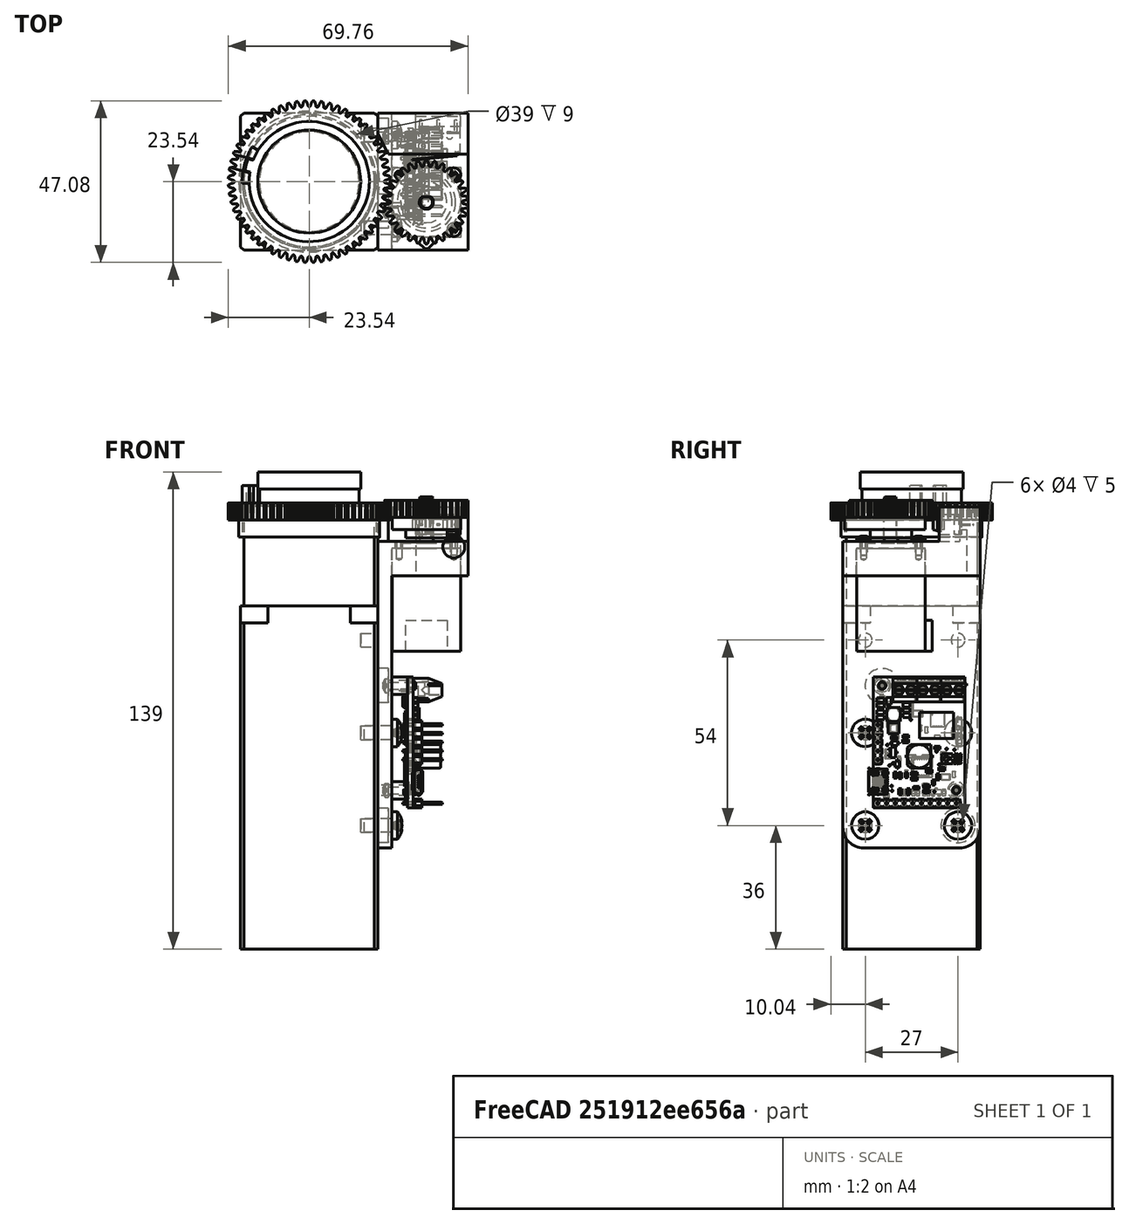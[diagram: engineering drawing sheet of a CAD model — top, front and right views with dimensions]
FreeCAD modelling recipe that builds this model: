
FCSTD DOCUMENT  (FreeCAD 0.19R23578 (Git))
Label: assembly-gear
License: All rights reserved
LicenseURL: http://en.wikipedia.org/wiki/All_rights_reserved
objects: Part::FeaturePython×15, App::FeaturePython×8
note: 15 computed .brp shape members not serialized (recipe doc carries the construction recipe); baked Part::Feature solids carry a one-line shape summary decoded from their .brp

FEATURE [Part::FeaturePython] b_microscope_001_  label="microscope_001"  # a2plus imported part (geometry in sourceFile) (typed FeaturePython)
  Visibility1 = true
  a2p_Version = V0.1
  fixedPosition = true
  objectType = a2pPart
  sourceFile = ./microscope.FCStd
  subassemblyImport = false
  timeLastImport = 1.60829e+09
  updateColors = true
FEATURE [Part::FeaturePython] b_motor_001_  label="motor_001"  # a2plus imported part (geometry in sourceFile) (typed FeaturePython)
  Placement = pos=(34.1,-6,-13.25) rot=(0,0,-1;1.5708rad)
  Visibility1 = true
  a2p_Version = V0.1
  fixedPosition = false
  objectType = a2pPart
  sourceFile = ./motor.FCStd
  subassemblyImport = false
  timeLastImport = 1.60829e+09
  updateColors = true
FEATURE [Part::FeaturePython] b_frame_001_  label="frame_001"  # a2plus imported part (geometry in sourceFile) (typed FeaturePython)
  Placement = pos=(20,-7.61e-14,18.75) rot=(0,0,1;0rad)
  Visibility1 = true
  a2p_Version = V0.1
  fixedPosition = false
  objectType = a2pPart
  sourceFile = ./frame.FCStd
  subassemblyImport = false
  timeLastImport = 1.60978e+09
  updateColors = true
FEATURE [Part::FeaturePython] b_D2FS_FL_N1_001_  label="D2FS_FL_N1_001"  # a2plus imported part (geometry in sourceFile) (typed FeaturePython)
  Placement = pos=(34.35,13,20.75) rot=(0,0,1;3.14159rad)
  Visibility1 = true
  a2p_Version = V0.1
  fixedPosition = false
  objectType = a2pPart
  sourceFile = ./D2FS_FL_N.step
  subassemblyImport = false
  timeLastImport = 1.60829e+09
  updateColors = true
FEATURE [Part::FeaturePython] b_tic834_001_  label="tic834_001"  # a2plus imported part (geometry in sourceFile) (typed FeaturePython)
  Placement = pos=(28.6611,15.54,-58.81) rot=(0.707107,0,0.707107;3.14159rad)
  Visibility1 = true
  a2p_Version = V0.1
  fixedPosition = false
  objectType = a2pPart
  sourceFile = ./tic834.FCStd
  subassemblyImport = false
  timeLastImport = 1.60829e+09
  updateColors = true
FEATURE [Part::FeaturePython] Screw  label="M2x4-Screw"  # Fasteners workbench fastener (typed FeaturePython)
  Placement = pos=(42.1,-14,18.75) rot=(0,0,1;0rad)
  Visibility1 = true
  diameter = 2
  invert = false
  length = 1
  lengthCustom = 4
  matchOuter = false
  offset = 0
  thread = false
  type = 33
FEATURE [Part::FeaturePython] Screw001  label="M2x4-Screw001"  # Fasteners workbench fastener (typed FeaturePython)
  Placement = pos=(42.1,2,18.75) rot=(0,0,1;0rad)
  Visibility1 = true
  diameter = 2
  invert = false
  length = 1
  lengthCustom = 4
  matchOuter = false
  offset = 0
  thread = false
  type = 33
FEATURE [Part::FeaturePython] Screw002  label="M2x8-Screw006"  # Fasteners workbench fastener (typed FeaturePython)
  Placement = pos=(23,-8.59,-23.25) rot=(-0.687002,-0.236764,0.687002;2.67663rad)
  Visibility1 = true
  diameter = 2
  invert = false
  length = 4
  lengthCustom = 8
  matchOuter = false
  offset = 0
  thread = false
  type = 33
FEATURE [Part::FeaturePython] Screw003  label="M4x8-Screw"  # Fasteners workbench fastener (typed FeaturePython)
  Placement = pos=(24,-13.5,-37) rot=(0,1,0;1.5708rad)
  Visibility1 = true
  diameter = 6
  invert = false
  length = 2
  lengthCustom = 8
  matchOuter = false
  offset = 0
  thread = false
  type = 33
FEATURE [Part::FeaturePython] Screw004  label="M4x8-Screw019"  # Fasteners workbench fastener (typed FeaturePython)
  Placement = pos=(24,13.5,-37) rot=(0,1,0;1.5708rad)
  Visibility1 = true
  diameter = 6
  invert = false
  length = 2
  lengthCustom = 8
  matchOuter = false
  offset = 0
  thread = false
  type = 33
FEATURE [Part::FeaturePython] Screw005  label="M4x8-Screw013"  # Fasteners workbench fastener (typed FeaturePython)
  Placement = pos=(24,13.5,-64) rot=(0,1,0;1.5708rad)
  Visibility1 = true
  diameter = 6
  invert = false
  length = 2
  lengthCustom = 8
  matchOuter = false
  offset = 0
  thread = false
  type = 33
FEATURE [Part::FeaturePython] Screw006  label="M4x8-Screw020"  # Fasteners workbench fastener (typed FeaturePython)
  Placement = pos=(24,-13.5,-64) rot=(0,1,0;1.5708rad)
  Visibility1 = true
  diameter = 6
  invert = false
  length = 2
  lengthCustom = 8
  matchOuter = false
  offset = 0
  thread = false
  type = 33
FEATURE [Part::FeaturePython] Screw007  label="M2x8-Screw"  # Fasteners workbench fastener (typed FeaturePython)
  Placement = pos=(23,13,-53.73) rot=(-0.687002,-0.236764,0.687002;2.67663rad)
  Visibility1 = true
  diameter = 2
  invert = false
  length = 4
  lengthCustom = 8
  matchOuter = false
  offset = 0
  thread = false
  type = 33
FEATURE [Part::FeaturePython] b_ring_gear_001_  label="ring-gear_001"  # a2plus imported part (geometry in sourceFile) (typed FeaturePython)
  Placement = pos=(1.33e-13,-2.8158e-12,30) rot=(0,0,1;6.02139rad)
  a2p_Version = V0.1
  fixedPosition = false
  objectType = a2pPart
  sourceFile = ./ring-gear.FCStd
  subassemblyImport = false
  timeLastImport = 1.60978e+09
  updateColors = true
FEATURE [App::FeaturePython] axisCoincident_004  label="axisCoincident_004__ring-gear_001"  # a2plus constraint (typed FeaturePython)
  Object1 = b_microscope_001_
  Object2 = b_ring_gear_001_
  ParentTreeObject = -> b_microscope_001_
  SubElement1 = Edge3
  SubElement2 = Edge5
  Suppressed = false
  Type = axial
  directionConstraint = 0
  lockRotation = false
FEATURE [App::FeaturePython] axisCoincident_004_mirror  label="axisCoincident_004__microscope_001"  # a2plus constraint (typed FeaturePython)
  Object1 = b_microscope_001_
  Object2 = b_ring_gear_001_
  ParentTreeObject = -> b_ring_gear_001_
  SubElement1 = Edge3
  SubElement2 = Edge5
  Suppressed = false
  Type = axial
  directionConstraint = 0
  lockRotation = false
FEATURE [Part::FeaturePython] b_pulley_gear_001_  label="pulley-gear_001"  # a2plus imported part (geometry in sourceFile) (typed FeaturePython)
  Placement = pos=(34.1,-6,19.75) rot=(0,0,-1;4.71239rad)
  a2p_Version = V0.1
  fixedPosition = false
  objectType = a2pPart
  sourceFile = ./pulley-gear.FCStd
  subassemblyImport = false
  timeLastImport = 1.60978e+09
  updateColors = true
FEATURE [App::FeaturePython] circularEdge_002  label="circularEdge_002__frame_001"  # a2plus constraint (typed FeaturePython)
  Object1 = b_microscope_001_
  Object2 = b_frame_001_
  ParentTreeObject = -> b_microscope_001_
  SubElement1 = Edge47
  SubElement2 = Edge12
  Suppressed = false
  Type = circularEdge
  directionConstraint = 1
  lockRotation = false
  offset = 0
FEATURE [App::FeaturePython] circularEdge_002_mirror  label="circularEdge_002__microscope_001"  # a2plus constraint (typed FeaturePython)
  Object1 = b_microscope_001_
  Object2 = b_frame_001_
  ParentTreeObject = -> b_frame_001_
  SubElement1 = Edge47
  SubElement2 = Edge12
  Suppressed = false
  Type = circularEdge
  directionConstraint = 1
  lockRotation = false
  offset = 0
FEATURE [App::FeaturePython] circularEdge_004  label="circularEdge_004__pulley-gear_001"  # a2plus constraint (typed FeaturePython)
  Object1 = b_motor_001_
  Object2 = b_pulley_gear_001_
  ParentTreeObject = -> b_motor_001_
  SubElement1 = Edge5
  SubElement2 = Edge932
  Suppressed = false
  Type = circularEdge
  directionConstraint = 1
  lockRotation = false
  offset = 0
FEATURE [App::FeaturePython] circularEdge_004_mirror  label="circularEdge_004__motor_001"  # a2plus constraint (typed FeaturePython)
  Object1 = b_motor_001_
  Object2 = b_pulley_gear_001_
  ParentTreeObject = -> b_pulley_gear_001_
  SubElement1 = Edge5
  SubElement2 = Edge932
  Suppressed = false
  Type = circularEdge
  directionConstraint = 1
  lockRotation = false
  offset = 0
FEATURE [App::FeaturePython] axisParallel_001  label="axisParallel_001__motor_001"  # a2plus constraint (typed FeaturePython)
  Object1 = b_pulley_gear_001_
  Object2 = b_motor_001_
  ParentTreeObject = -> b_pulley_gear_001_
  SubElement1 = Edge934
  SubElement2 = Edge12
  Suppressed = false
  Type = axisParallel
  directionConstraint = 0
FEATURE [App::FeaturePython] axisParallel_001_mirror  label="axisParallel_001__pulley-gear_001"  # a2plus constraint (typed FeaturePython)
  Object1 = b_pulley_gear_001_
  Object2 = b_motor_001_
  ParentTreeObject = -> b_motor_001_
  SubElement1 = Edge934
  SubElement2 = Edge12
  Suppressed = false
  Type = axisParallel
  directionConstraint = 0
